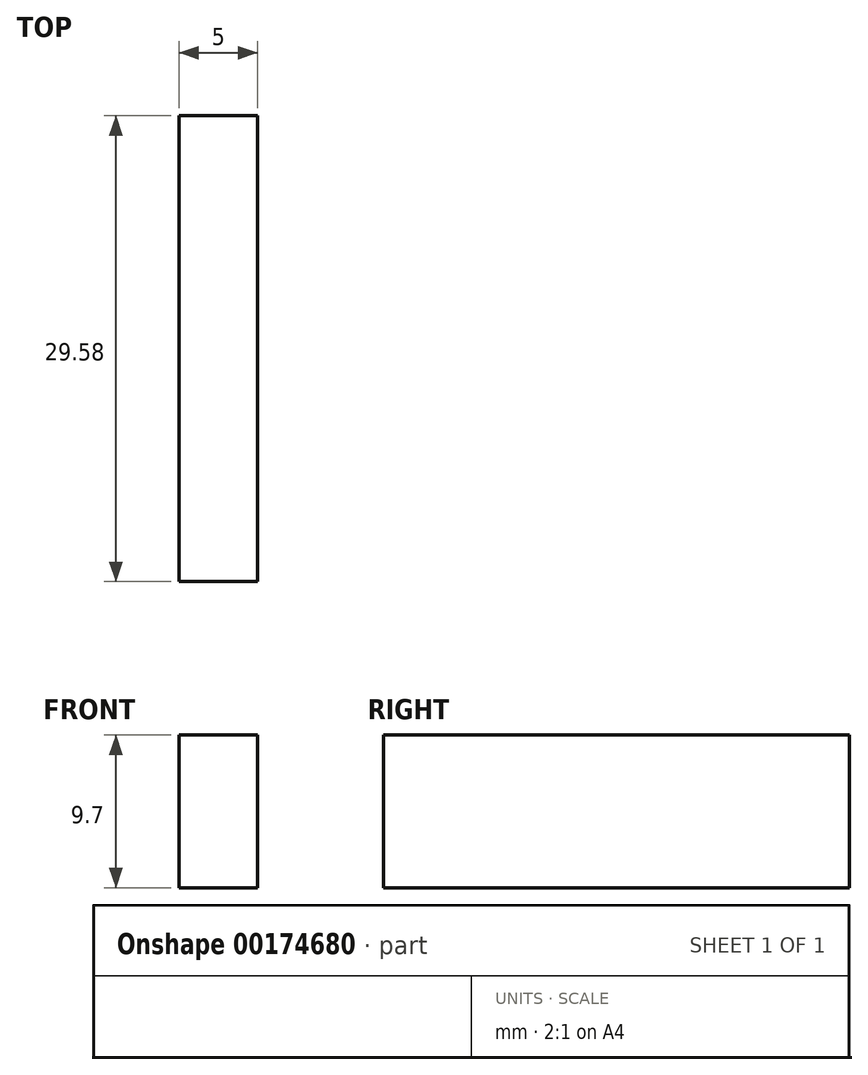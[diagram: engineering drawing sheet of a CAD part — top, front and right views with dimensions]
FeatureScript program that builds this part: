
annotation { "Feature Type Name" : "Feature", "Feature Type Description" : "" }
export const myFeature = defineFeature(function(context is Context, id is Id, definition is map)
    precondition{}
    {
        {
            var Q0;
            Q0=qCreatedBy(makeId("Right.planeOp"),FACE);
            cPlane(context, id + "F0", {"entities" : qUnion([Q0]), "cplaneType" : CPlaneType.OFFSET, "offset" : 87.5 * mm, "oppositeDirection" : true, "width" : 150 * mm, "height" : 150 * mm});
        }
        {
            var Q0;
            Q0=qCreatedBy(id+"F0.planeOp",FACE);
            var sketch = newSketch(context, id + "F1", { "sketchPlane" : qUnion([Q0])});
            skLineSegment(sketch, "E0", {"start": v(-42.5, 9.5) * mm, "end": v(-42.5, -9.5) * mm});
            skLineSegment(sketch, "E1", {"start": v(-42.5, -9.5) * mm, "end": v(42.5, -9.5) * mm});
            skLineSegment(sketch, "E2", {"start": v(42.5, -9.5) * mm, "end": v(42.5, 9.5) * mm});
            skLineSegment(sketch, "E3", {"start": v(42.5, 9.5) * mm, "end": v(-42.5, 9.5) * mm});
            skLineSegment(sketch, "E4", {"start": v(0.9, -3.7) * mm, "end": v(0.9, 6) * mm});
            skLineSegment(sketch, "E5", {"start": v(0.9, 6) * mm, "end": v(30.48, 6) * mm});
            skLineSegment(sketch, "E6", {"start": v(30.48, 6) * mm, "end": v(30.48, -3.7) * mm});
            skLineSegment(sketch, "E7", {"start": v(30.48, -3.7) * mm, "end": v(0.9, -3.7) * mm});
            skLineSegment(sketch, "E8", {"start": v(-0.9, -3.7) * mm, "end": v(-0.9, 6) * mm});
            skLineSegment(sketch, "E9", {"start": v(-0.9, 6) * mm, "end": v(-30.48, 6) * mm});
            skLineSegment(sketch, "E10", {"start": v(-30.48, 6) * mm, "end": v(-30.48, -3.7) * mm});
            skLineSegment(sketch, "E11", {"start": v(-30.48, -3.7) * mm, "end": v(-0.9, -3.7) * mm});
            skSolve(sketch);
        }
        {
            var Q0;
            Q0=makeQuery(id+"F1.imprint","IMPRINT",FACE,{"disambiguationData":[TD([[makeQuery(id+"F1.imprint","IMPRINT",EDGE,{"derivedFrom":sQuery(id+"F1.wireOp",EDGE,"E8")}),1.0]])]});
            extrude(context, id + "F2", {"entities" : qUnion([Q0]), "depth" : 5 * mm});
        }
    });
